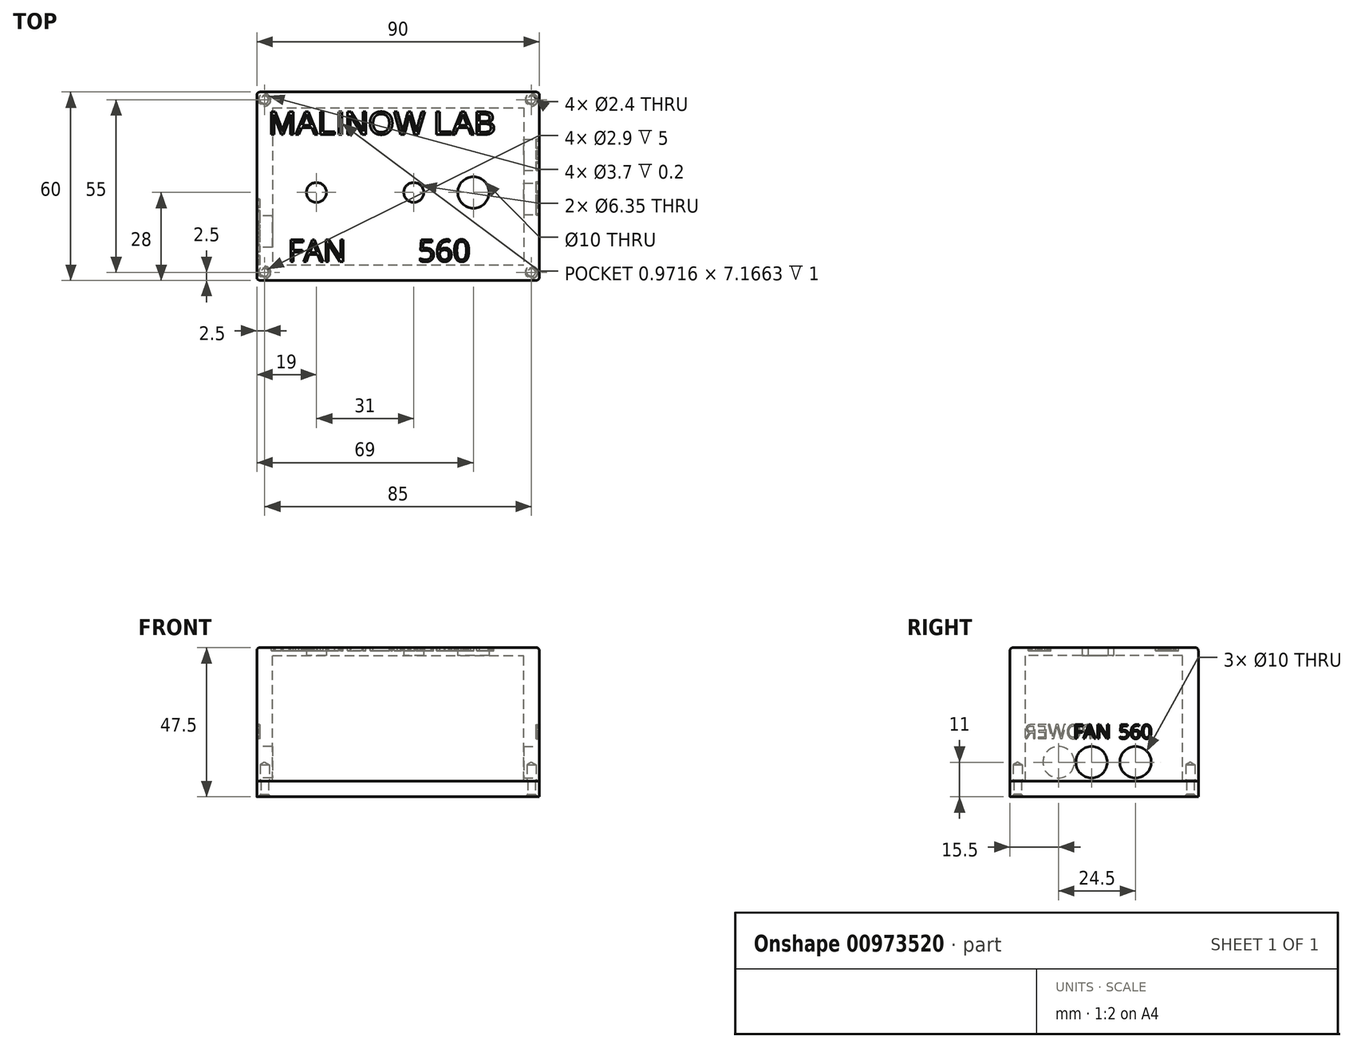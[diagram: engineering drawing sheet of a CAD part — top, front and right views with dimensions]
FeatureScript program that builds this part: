
annotation { "Feature Type Name" : "Feature", "Feature Type Description" : "" }
export const myFeature = defineFeature(function(context is Context, id is Id, definition is map)
    precondition{}
    {
        {
            var Q0;
            Q0=qCreatedBy(makeId("Top.planeOp"),FACE);
            var sketch = newSketch(context, id + "F0", { "sketchPlane" : qUnion([Q0])});
            skLineSegment(sketch, "E0.bottom", {"start": v(0, 0) * mm, "end": v(90, 0) * mm});
            skLineSegment(sketch, "E0.top", {"start": v(0, 60) * mm, "end": v(90, 60) * mm});
            skLineSegment(sketch, "E0.left", {"start": v(0, 0) * mm, "end": v(0, 60) * mm});
            skLineSegment(sketch, "E0.right", {"start": v(90, 0) * mm, "end": v(90, 60) * mm});
            skCircle(sketch, "E1", {"center": v(69, 28) * mm, "radius": 5 * mm});
            skCircle(sketch, "E2", {"center": v(19, 28) * mm, "radius": 3.18 * mm});
            skLineSegment(sketch, "E3", {"start": v(5, 60) * mm, "end": v(5, 5) * mm, "construction": true});
            skLineSegment(sketch, "E4", {"start": v(5, 5) * mm, "end": v(85, 5) * mm, "construction": true});
            skLineSegment(sketch, "E5", {"start": v(85, 5) * mm, "end": v(85, 60) * mm, "construction": true});
            skLineSegment(sketch, "E6", {"start": v(0, 55) * mm, "end": v(90, 55) * mm, "construction": true});
            skLineSegment(sketch, "E7", {"start": v(5, 5) * mm, "end": v(0, 5) * mm, "construction": true});
            skLineSegment(sketch, "E8", {"start": v(85, 5) * mm, "end": v(90, 5) * mm, "construction": true});
            skPoint(sketch, "E9.endSnap0", {"position": v(5, 32.5) * mm});
            skLineSegment(sketch, "E10", {"start": v(5, 60) * mm, "end": v(85, 55) * mm, "construction": true});
            skLineSegment(sketch, "E11", {"start": v(85, 60) * mm, "end": v(5, 55) * mm, "construction": true});
            skLineSegment(sketch, "E12", {"start": v(90, 5) * mm, "end": v(0, 0) * mm, "construction": true});
            skLineSegment(sketch, "E13", {"start": v(0, 5) * mm, "end": v(90, 0) * mm, "construction": true});
            skPoint(sketch, "E14", {"position": v(45, 2.5) * mm});
            skPoint(sketch, "E15", {"position": v(45, 57.5) * mm});
            skLineSegment(sketch, "E16", {"start": v(5, 28) * mm, "end": v(85, 28) * mm, "construction": true});
            skCircle(sketch, "E17", {"center": v(50, 28) * mm, "radius": 3.18 * mm});
            skSolve(sketch);
        }
        {
            var Q0;
            Q0=makeQuery(id+"F0.imprint","IMPRINT",FACE,{"disambiguationData":[TD([[makeQuery(id+"F0.imprint","IMPRINT",EDGE,{"derivedFrom":sQuery(id+"F0.wireOp",EDGE,"E0.bottom")}),1.0]])]});
            extrude(context, id + "F1", {"entities" : qUnion([Q0]), "depth" : 2.5 * mm, "offsetDistance" : 25 * mm});
        }
        {
            var Q0;
            Q0=makeQuery(id+"F1.opExtrude","CAP_FACE",FACE,{"disambiguationData":[OSD([sQuery(id+"F0.wireOp",EDGE,"E0.bottom"),sQuery(id+"F0.wireOp",EDGE,"E0.top"),sQuery(id+"F0.wireOp",EDGE,"E0.left"),sQuery(id+"F0.wireOp",EDGE,"E0.right"),sQuery(id+"F0.wireOp",EDGE,"692mbZP9-ke58-QfXx-eCDH-dWQCKjaEO8YG"),sQuery(id+"F0.wireOp",EDGE,"E1"),sQuery(id+"F0.wireOp",EDGE,"E2")])],"isStart":true});
            var sketch = newSketch(context, id + "F2", { "sketchPlane" : qUnion([Q0])});
            skLineSegment(sketch, "E18.bottom", {"start": v(0, -60) * mm, "end": v(90, -60) * mm, "construction": true});
            skLineSegment(sketch, "E18.top", {"start": v(0, 0) * mm, "end": v(90, 0) * mm, "construction": true});
            skLineSegment(sketch, "E18.left", {"start": v(0, -60) * mm, "end": v(0, 0) * mm, "construction": true});
            skLineSegment(sketch, "E18.right", {"start": v(90, -60) * mm, "end": v(90, 0) * mm, "construction": true});
            skLineSegment(sketch, "E19.bottom", {"start": v(5, -55) * mm, "end": v(85, -55) * mm});
            skLineSegment(sketch, "E19.top", {"start": v(5, -5) * mm, "end": v(85, -5) * mm});
            skLineSegment(sketch, "E19.left", {"start": v(5, -55) * mm, "end": v(5, -5) * mm});
            skLineSegment(sketch, "E19.right", {"start": v(85, -55) * mm, "end": v(85, -5) * mm});
            skSolve(sketch);
        }
        {
            var Q0;
            Q0=makeQuery(id+"F2.imprint","IMPRINT",FACE,{"disambiguationData":[TD([[makeQuery(id+"F2.imprint","IMPRINT",EDGE,{"derivedFrom":sQuery(id+"F2.wireOp",EDGE,"E19.bottom")}),-1.0]])]});
            var Q1;
            Q1=makeQuery(id+"F2.imprint","IMPRINT",FACE,{"disambiguationData":[TD([[makeQuery(id+"F2.imprint","IMPRINT",EDGE,{"derivedFrom":makeQuery(id+"FxvTJw6m9mzOm3c_1.hole-0.boolean.opBoolean","INTERSECT",EDGE,{"derivedFrom":[makeQuery(id+"F1.opExtrude","CAP_FACE",FACE,{"disambiguationData":[OSD([sQuery(id+"F0.wireOp",EDGE,"E0.bottom"),sQuery(id+"F0.wireOp",EDGE,"E0.top"),sQuery(id+"F0.wireOp",EDGE,"E0.left"),sQuery(id+"F0.wireOp",EDGE,"E0.right"),sQuery(id+"F0.wireOp",EDGE,"692mbZP9-ke58-QfXx-eCDH-dWQCKjaEO8YG"),sQuery(id+"F0.wireOp",EDGE,"E1"),sQuery(id+"F0.wireOp",EDGE,"E2")])],"isStart":true}),makeQuery(id+"FxvTJw6m9mzOm3c_1.hole-0.opRevolve","SWEPT_FACE",FACE,{"disambiguationData":[OSD([sQuery(id+"FxvTJw6m9mzOm3c_1.hole-0.sketch.wireOp",EDGE,"core_line_2")])]})]})}),1.0]])]});
            var Q2;
            Q2=makeQuery(id+"F2.imprint","IMPRINT",FACE,{"disambiguationData":[TD([[makeQuery(id+"F2.imprint","IMPRINT",EDGE,{"derivedFrom":makeQuery(id+"FxvTJw6m9mzOm3c_1.hole-1.boolean.opBoolean","INTERSECT",EDGE,{"derivedFrom":[makeQuery(id+"F1.opExtrude","CAP_FACE",FACE,{"disambiguationData":[OSD([sQuery(id+"F0.wireOp",EDGE,"E0.bottom"),sQuery(id+"F0.wireOp",EDGE,"E0.top"),sQuery(id+"F0.wireOp",EDGE,"E0.left"),sQuery(id+"F0.wireOp",EDGE,"E0.right"),sQuery(id+"F0.wireOp",EDGE,"692mbZP9-ke58-QfXx-eCDH-dWQCKjaEO8YG"),sQuery(id+"F0.wireOp",EDGE,"E1"),sQuery(id+"F0.wireOp",EDGE,"E2")])],"isStart":true}),makeQuery(id+"FxvTJw6m9mzOm3c_1.hole-1.opRevolve","SWEPT_FACE",FACE,{"disambiguationData":[OSD([sQuery(id+"FxvTJw6m9mzOm3c_1.hole-1.sketch.wireOp",EDGE,"core_line_2")])]})]})}),1.0]])]});
            var Q3;
            Q3=makeQuery(id+"F2.imprint","IMPRINT",FACE,{"disambiguationData":[TD([[makeQuery(id+"F2.imprint","IMPRINT",EDGE,{"derivedFrom":makeQuery(id+"FxvTJw6m9mzOm3c_1.hole-2.boolean.opBoolean","INTERSECT",EDGE,{"derivedFrom":[makeQuery(id+"F1.opExtrude","CAP_FACE",FACE,{"disambiguationData":[OSD([sQuery(id+"F0.wireOp",EDGE,"E0.bottom"),sQuery(id+"F0.wireOp",EDGE,"E0.top"),sQuery(id+"F0.wireOp",EDGE,"E0.left"),sQuery(id+"F0.wireOp",EDGE,"E0.right"),sQuery(id+"F0.wireOp",EDGE,"692mbZP9-ke58-QfXx-eCDH-dWQCKjaEO8YG"),sQuery(id+"F0.wireOp",EDGE,"E1"),sQuery(id+"F0.wireOp",EDGE,"E2")])],"isStart":true}),makeQuery(id+"FxvTJw6m9mzOm3c_1.hole-2.opRevolve","SWEPT_FACE",FACE,{"disambiguationData":[OSD([sQuery(id+"FxvTJw6m9mzOm3c_1.hole-2.sketch.wireOp",EDGE,"core_line_2")])]})]})}),1.0]])]});
            var Q4;
            Q4=makeQuery(id+"F2.imprint","IMPRINT",FACE,{"disambiguationData":[TD([[makeQuery(id+"F2.imprint","IMPRINT",EDGE,{"derivedFrom":makeQuery(id+"FxvTJw6m9mzOm3c_1.hole-3.boolean.opBoolean","INTERSECT",EDGE,{"derivedFrom":[makeQuery(id+"F1.opExtrude","CAP_FACE",FACE,{"disambiguationData":[OSD([sQuery(id+"F0.wireOp",EDGE,"E0.bottom"),sQuery(id+"F0.wireOp",EDGE,"E0.top"),sQuery(id+"F0.wireOp",EDGE,"E0.left"),sQuery(id+"F0.wireOp",EDGE,"E0.right"),sQuery(id+"F0.wireOp",EDGE,"692mbZP9-ke58-QfXx-eCDH-dWQCKjaEO8YG"),sQuery(id+"F0.wireOp",EDGE,"E1"),sQuery(id+"F0.wireOp",EDGE,"E2")])],"isStart":true}),makeQuery(id+"FxvTJw6m9mzOm3c_1.hole-3.opRevolve","SWEPT_FACE",FACE,{"disambiguationData":[OSD([sQuery(id+"FxvTJw6m9mzOm3c_1.hole-3.sketch.wireOp",EDGE,"core_line_2")])]})]})}),1.0]])]});
            extrude(context, id + "F3", {"entities" : qUnion([Q0, Q1, Q2, Q3, Q4]), "depth" : 40 * mm, "offsetDistance" : 25 * mm});
        }
        {
            var Q0;
            Q0=makeQuery(id+"F3.opExtrude","CAP_FACE",FACE,{"disambiguationData":[OSD([sQuery(id+"F0.wireOp",EDGE,"E0.bottom"),sQuery(id+"F0.wireOp",EDGE,"E0.top"),sQuery(id+"F0.wireOp",EDGE,"E0.left"),sQuery(id+"F0.wireOp",EDGE,"E0.right"),sQuery(id+"F2.wireOp",EDGE,"E19.bottom"),sQuery(id+"F2.wireOp",EDGE,"E19.top"),sQuery(id+"F2.wireOp",EDGE,"E19.left"),sQuery(id+"F2.wireOp",EDGE,"E19.right")])],"isStart":false});
            var sketch = newSketch(context, id + "F4", { "sketchPlane" : qUnion([Q0])});
            skLineSegment(sketch, "E20.bottom", {"start": v(0, 0) * mm, "end": v(90, 0) * mm});
            skLineSegment(sketch, "E20.top", {"start": v(0, -60) * mm, "end": v(90, -60) * mm});
            skLineSegment(sketch, "E20.left", {"start": v(0, 0) * mm, "end": v(0, -60) * mm});
            skLineSegment(sketch, "E20.right", {"start": v(90, 0) * mm, "end": v(90, -60) * mm});
            skLineSegment(sketch, "E21.bottom", {"start": v(5, -5) * mm, "end": v(85, -5) * mm, "construction": true});
            skLineSegment(sketch, "E21.top", {"start": v(5, -55) * mm, "end": v(85, -55) * mm, "construction": true});
            skLineSegment(sketch, "E21.left", {"start": v(5, -5) * mm, "end": v(5, -55) * mm, "construction": true});
            skLineSegment(sketch, "E21.right", {"start": v(85, -5) * mm, "end": v(85, -55) * mm, "construction": true});
            skSolve(sketch);
        }
        {
            var Q0;
            Q0=makeQuery(id+"F4.imprint","IMPRINT",FACE,{"disambiguationData":[TD([[makeQuery(id+"F4.imprint","IMPRINT",EDGE,{"derivedFrom":sQuery(id+"F4.wireOp",EDGE,"E20.bottom")}),-1.0]])]});
            var Q1;
            Q1=makeQuery(id+"F4.imprint","IMPRINT",FACE,{"disambiguationData":[TD([[makeQuery(id+"F4.imprint","IMPRINT",EDGE,{"derivedFrom":makeQuery(id+"F3.opExtrude","CAP_EDGE",EDGE,{"disambiguationData":[OSD([sQuery(id+"F2.wireOp",EDGE,"E19.bottom")])],"isStart":false})}),1.0]])]});
            extrude(context, id + "F5", {"entities" : qUnion([Q0, Q1]), "depth" : 5 * mm, "offsetDistance" : 25 * mm});
        }
        {
            var Q0;
            Q0=makeQuery(id+"F5.opExtrude","CAP_FACE",FACE,{"disambiguationData":[OSD([sQuery(id+"F4.wireOp",EDGE,"E20.bottom"),sQuery(id+"F4.wireOp",EDGE,"E20.top"),sQuery(id+"F4.wireOp",EDGE,"E20.left"),sQuery(id+"F4.wireOp",EDGE,"E20.right")])],"isStart":false});
            var sketch = newSketch(context, id + "F6", { "sketchPlane" : qUnion([Q0])});
            skLineSegment(sketch, "E22.bottom", {"start": v(0, -60) * mm, "end": v(90, -60) * mm, "construction": true});
            skLineSegment(sketch, "E22.top", {"start": v(0, 0) * mm, "end": v(90, 0) * mm, "construction": true});
            skLineSegment(sketch, "E22.left", {"start": v(0, -60) * mm, "end": v(0, 0) * mm, "construction": true});
            skLineSegment(sketch, "E22.right", {"start": v(90, -60) * mm, "end": v(90, 0) * mm, "construction": true});
            skLineSegment(sketch, "E23.bottom", {"start": v(5, -55) * mm, "end": v(85, -55) * mm, "construction": true});
            skLineSegment(sketch, "E23.top", {"start": v(5, -5) * mm, "end": v(85, -5) * mm, "construction": true});
            skLineSegment(sketch, "E23.left", {"start": v(5, -55) * mm, "end": v(5, -5) * mm, "construction": true});
            skLineSegment(sketch, "E23.right", {"start": v(85, -55) * mm, "end": v(85, -5) * mm, "construction": true});
            skLineSegment(sketch, "E24", {"start": v(5, -5) * mm, "end": v(0, 0) * mm, "construction": true});
            skLineSegment(sketch, "E25", {"start": v(85, -5) * mm, "end": v(90, 0) * mm, "construction": true});
            skLineSegment(sketch, "E26", {"start": v(85, -55) * mm, "end": v(90, -60) * mm, "construction": true});
            skLineSegment(sketch, "E27", {"start": v(5, -55) * mm, "end": v(0, -60) * mm, "construction": true});
            skPoint(sketch, "E28", {"position": v(2.5, -2.5) * mm});
            skPoint(sketch, "E29", {"position": v(87.5, -2.5) * mm});
            skPoint(sketch, "E30", {"position": v(87.5, -57.5) * mm});
            skPoint(sketch, "E31", {"position": v(2.5, -57.5) * mm});
            skSolve(sketch);
        }
        {
            var Q0;
            Q0=sQuery(id+"F6.wireOp",VERTEX,"E28");
            var Q1;
            Q1=sQuery(id+"F6.wireOp",VERTEX,"E31");
            var Q2;
            Q2=sQuery(id+"F6.wireOp",VERTEX,"E30");
            var Q3;
            Q3=sQuery(id+"F6.wireOp",VERTEX,"E29");
            var Q4;
            Q4=makeQuery(id+"F3.opExtrude","SWEPT_BODY",BODY,{"disambiguationData":[OSD([sQuery(id+"F0.wireOp",EDGE,"E0.bottom"),sQuery(id+"F0.wireOp",EDGE,"E0.top"),sQuery(id+"F0.wireOp",EDGE,"E0.left"),sQuery(id+"F0.wireOp",EDGE,"E0.right"),sQuery(id+"F2.wireOp",EDGE,"E19.bottom"),sQuery(id+"F2.wireOp",EDGE,"E19.top"),sQuery(id+"F2.wireOp",EDGE,"E19.left"),sQuery(id+"F2.wireOp",EDGE,"E19.right")])]});
            var Q5;
            Q5=makeQuery(id+"F5.opExtrude","SWEPT_BODY",BODY,{"disambiguationData":[OSD([sQuery(id+"F4.wireOp",EDGE,"E20.bottom"),sQuery(id+"F4.wireOp",EDGE,"E20.top"),sQuery(id+"F4.wireOp",EDGE,"E20.left"),sQuery(id+"F4.wireOp",EDGE,"E20.right")])]});
            hole(context, id + "F7", {"style" : HoleStyle.C_SINK, "endStyle" : HoleEndStyle.BLIND, "holeDiameter" : 2.4 * mm, "cSinkDiameter" : 4 * mm, "cSinkAngle" : 90 * degree, "majorDiameter" : 5 * mm, "holeDepth" : 5 * mm, "isTappedThrough" : true, "tappedDepth" : 12 * mm, "tapClearance" : 3, "locations" : qUnion([Q0, Q1, Q2, Q3]), "scope" : qUnion([Q4, Q5])});
        }
        {
            var Q0;
            Q0=makeQuery(id+"F3.opExtrude","CAP_FACE",FACE,{"disambiguationData":[OSD([sQuery(id+"F0.wireOp",EDGE,"E0.bottom"),sQuery(id+"F0.wireOp",EDGE,"E0.top"),sQuery(id+"F0.wireOp",EDGE,"E0.left"),sQuery(id+"F0.wireOp",EDGE,"E0.right"),sQuery(id+"F2.wireOp",EDGE,"E19.bottom"),sQuery(id+"F2.wireOp",EDGE,"E19.top"),sQuery(id+"F2.wireOp",EDGE,"E19.left"),sQuery(id+"F2.wireOp",EDGE,"E19.right")])],"isStart":false});
            var sketch = newSketch(context, id + "F8", { "sketchPlane" : qUnion([Q0])});
            skPoint(sketch, "E32", {"position": v(2.5, -2.5) * mm});
            skPoint(sketch, "E33", {"position": v(2.5, -57.5) * mm});
            skPoint(sketch, "E34", {"position": v(87.5, -57.5) * mm});
            skPoint(sketch, "E35", {"position": v(87.5, -2.5) * mm});
            skSolve(sketch);
        }
        {
            var Q0;
            Q0=sQuery(id+"F8.wireOp",VERTEX,"E32");
            var Q1;
            Q1=sQuery(id+"F8.wireOp",VERTEX,"E33");
            var Q2;
            Q2=sQuery(id+"F8.wireOp",VERTEX,"E34");
            var Q3;
            Q3=sQuery(id+"F8.wireOp",VERTEX,"E35");
            var Q4;
            Q4=makeQuery(id+"F3.opExtrude","SWEPT_BODY",BODY,{"disambiguationData":[OSD([sQuery(id+"F0.wireOp",EDGE,"E0.bottom"),sQuery(id+"F0.wireOp",EDGE,"E0.top"),sQuery(id+"F0.wireOp",EDGE,"E0.left"),sQuery(id+"F0.wireOp",EDGE,"E0.right"),sQuery(id+"F2.wireOp",EDGE,"E19.bottom"),sQuery(id+"F2.wireOp",EDGE,"E19.top"),sQuery(id+"F2.wireOp",EDGE,"E19.left"),sQuery(id+"F2.wireOp",EDGE,"E19.right")])]});
            hole(context, id + "F9", {"style" : HoleStyle.C_BORE, "endStyle" : HoleEndStyle.BLIND, "holeDiameter" : 2.9 * mm, "cBoreDiameter" : 3.7 * mm, "cBoreDepth" : .2 * mm, "majorDiameter" : 5 * mm, "holeDepth" : 5.2 * mm, "isTappedThrough" : true, "tappedDepth" : 12 * mm, "tapClearance" : 3, "locations" : qUnion([Q0, Q1, Q2, Q3]), "scope" : qUnion([Q4])});
        }
        {
            var Q0;
            Q0=makeQuery(id+"F1.opExtrude","CAP_EDGE",EDGE,{"disambiguationData":[OSD([sQuery(id+"F0.wireOp",EDGE,"E0.bottom")])],"isStart":false});
            var Q1;
            Q1=makeQuery(id+"F1.opExtrude","CAP_EDGE",EDGE,{"disambiguationData":[OSD([sQuery(id+"F0.wireOp",EDGE,"E0.left")])],"isStart":false});
            var Q2;
            Q2=makeQuery(id+"F1.opExtrude","CAP_EDGE",EDGE,{"disambiguationData":[OSD([sQuery(id+"F0.wireOp",EDGE,"E0.top")])],"isStart":false});
            var Q3;
            Q3=makeQuery(id+"F1.opExtrude","CAP_EDGE",EDGE,{"disambiguationData":[OSD([sQuery(id+"F0.wireOp",EDGE,"E0.right")])],"isStart":false});
            var Q4;
            Q4=makeQuery(id+"F3.opExtrude","SWEPT_EDGE",EDGE,{"disambiguationData":[OSD([sQuery(id+"F0.wireOp",EDGE,"E0.bottom"),sQuery(id+"F0.wireOp",EDGE,"E0.right")])]});
            var Q5;
            Q5=makeQuery(id+"F3.opExtrude","SWEPT_EDGE",EDGE,{"disambiguationData":[OSD([sQuery(id+"F0.wireOp",EDGE,"E0.bottom"),sQuery(id+"F0.wireOp",EDGE,"E0.left")])]});
            var Q6;
            Q6=makeQuery(id+"F1.opExtrude","SWEPT_EDGE",EDGE,{"disambiguationData":[OSD([sQuery(id+"F0.wireOp",EDGE,"E0.bottom"),sQuery(id+"F0.wireOp",EDGE,"E0.left")])]});
            var Q7;
            Q7=makeQuery(id+"F1.opExtrude","SWEPT_EDGE",EDGE,{"disambiguationData":[OSD([sQuery(id+"F0.wireOp",EDGE,"E0.bottom"),sQuery(id+"F0.wireOp",EDGE,"E0.right")])]});
            var Q8;
            Q8=makeQuery(id+"F3.opExtrude","SWEPT_EDGE",EDGE,{"disambiguationData":[OSD([sQuery(id+"F0.wireOp",EDGE,"E0.top"),sQuery(id+"F0.wireOp",EDGE,"E0.right")])]});
            var Q9;
            Q9=makeQuery(id+"F1.opExtrude","SWEPT_EDGE",EDGE,{"disambiguationData":[OSD([sQuery(id+"F0.wireOp",EDGE,"E0.top"),sQuery(id+"F0.wireOp",EDGE,"E0.right")])]});
            var Q10;
            Q10=makeQuery(id+"F3.opExtrude","SWEPT_EDGE",EDGE,{"disambiguationData":[OSD([sQuery(id+"F0.wireOp",EDGE,"E0.top"),sQuery(id+"F0.wireOp",EDGE,"E0.left")])]});
            var Q11;
            Q11=makeQuery(id+"F1.opExtrude","SWEPT_EDGE",EDGE,{"disambiguationData":[OSD([sQuery(id+"F0.wireOp",EDGE,"E0.top"),sQuery(id+"F0.wireOp",EDGE,"E0.left")])]});
            var Q12;
            Q12=makeQuery(id+"F5.opExtrude","SWEPT_EDGE",EDGE,{"disambiguationData":[OSD([sQuery(id+"F4.wireOp",EDGE,"E20.top"),sQuery(id+"F4.wireOp",EDGE,"E20.left")])]});
            var Q13;
            Q13=makeQuery(id+"F5.opExtrude","SWEPT_EDGE",EDGE,{"disambiguationData":[OSD([sQuery(id+"F4.wireOp",EDGE,"E20.bottom"),sQuery(id+"F4.wireOp",EDGE,"E20.left")])]});
            var Q14;
            Q14=makeQuery(id+"F5.opExtrude","SWEPT_EDGE",EDGE,{"disambiguationData":[OSD([sQuery(id+"F4.wireOp",EDGE,"E20.top"),sQuery(id+"F4.wireOp",EDGE,"E20.right")])]});
            var Q15;
            Q15=makeQuery(id+"F5.opExtrude","SWEPT_EDGE",EDGE,{"disambiguationData":[OSD([sQuery(id+"F4.wireOp",EDGE,"E20.bottom"),sQuery(id+"F4.wireOp",EDGE,"E20.right")])]});
            fillet(context, id + "F10", {"entities" : qUnion([Q0, Q1, Q2, Q3, Q4, Q5, Q6, Q7, Q8, Q9, Q10, Q11, Q12, Q13, Q14, Q15]), "radius" : 1 * mm, "tangentPropagation" : true, "allowEdgeOverflow" : false});
        }
        {
            var Q0;
            Q0=makeQuery(id+"F3.opExtrude","SWEPT_FACE",FACE,{"disambiguationData":[OSD([sQuery(id+"F0.wireOp",EDGE,"E0.left")])]});
            var sketch = newSketch(context, id + "F11", { "sketchPlane" : qUnion([Q0])});
            skCircle(sketch, "E36", {"center": v(-15.5, -34) * mm, "radius": 5 * mm});
            skLineSegment(sketch, "E37", {"start": v(-30, -40) * mm, "end": v(-30, 0) * mm, "construction": true});
            skLineSegment(sketch, "E38", {"start": v(-30, 0) * mm, "end": v(-1, -40) * mm, "construction": true});
            skLineSegment(sketch, "E39", {"start": v(-15.5, -20) * mm, "end": v(-15.5, -40) * mm, "construction": true});
            skLineSegment(sketch, "E40", {"start": v(-15.5, -40) * mm, "end": v(-15.5, 0) * mm, "construction": true});
            skSolve(sketch);
        }
        {
            var Q0;
            Q0=makeQuery(id+"F11.imprint","IMPRINT",FACE,{"disambiguationData":[TD([[makeQuery(id+"F11.imprint","IMPRINT",EDGE,{"derivedFrom":sQuery(id+"F11.wireOp",EDGE,"E36")}),1.0]])]});
            extrude(context, id + "F12", {"entities" : qUnion([Q0]), "operationType" : NewBodyOperationType.REMOVE, "endBound" : BoundingType.UP_TO_NEXT, "oppositeDirection" : true, "depth" : 25 * mm, "offsetDistance" : 25 * mm});
        }
        {
            var Q0;
            Q0=makeQuery(id+"F3.opExtrude","SWEPT_FACE",FACE,{"disambiguationData":[OSD([sQuery(id+"F0.wireOp",EDGE,"E0.right")])]});
            var sketch = newSketch(context, id + "F13", { "sketchPlane" : qUnion([Q0])});
            skLineSegment(sketch, "E41", {"start": v(1, -34) * mm, "end": v(59, -34) * mm, "construction": true});
            skCircle(sketch, "E42", {"center": v(26, -34) * mm, "radius": 5 * mm});
            skCircle(sketch, "E43", {"center": v(40, -34) * mm, "radius": 5 * mm});
            skSolve(sketch);
        }
        {
            var Q0;
            Q0=makeQuery(id+"F13.imprint","IMPRINT",FACE,{"disambiguationData":[TD([[makeQuery(id+"F13.imprint","IMPRINT",EDGE,{"derivedFrom":sQuery(id+"F13.wireOp",EDGE,"E42")}),1.0]])]});
            var Q1;
            Q1=makeQuery(id+"F13.imprint","IMPRINT",FACE,{"disambiguationData":[TD([[makeQuery(id+"F13.imprint","IMPRINT",EDGE,{"derivedFrom":sQuery(id+"F13.wireOp",EDGE,"E43")}),1.0]])]});
            var Q2;
            Q2=makeQuery(id+"F13.imprint","IMPRINT",FACE,{"disambiguationData":[TD([[makeQuery(id+"F13.imprint","IMPRINT",EDGE,{"derivedFrom":sQuery(id+"F13.wireOp",EDGE,"z5ahbYnX-TxnG-AjFd-NFLQ-6TXHqK5QM6zY")}),1.0]])]});
            extrude(context, id + "F14", {"entities" : qUnion([Q0, Q1, Q2]), "operationType" : NewBodyOperationType.REMOVE, "endBound" : BoundingType.UP_TO_NEXT, "oppositeDirection" : true, "depth" : 25 * mm, "offsetDistance" : 25 * mm});
        }
        {
            var Q0;
            Q0=makeQuery(id+"F10.opFillet","SPLIT",FACE,{"disambiguationData":[OD(4.0)],"derivedFrom":makeQuery(id+"F1.opExtrude","CAP_FACE",FACE,{"disambiguationData":[OSD([sQuery(id+"F0.wireOp",EDGE,"E0.bottom"),sQuery(id+"F0.wireOp",EDGE,"E0.top"),sQuery(id+"F0.wireOp",EDGE,"E0.left"),sQuery(id+"F0.wireOp",EDGE,"E0.right"),sQuery(id+"F0.wireOp",EDGE,"692mbZP9-ke58-QfXx-eCDH-dWQCKjaEO8YG"),sQuery(id+"F0.wireOp",EDGE,"E1"),sQuery(id+"F0.wireOp",EDGE,"E2")])],"isStart":false})});
            var sketch = newSketch(context, id + "F15", { "sketchPlane" : qUnion([Q0])});
            skLineSegment(sketch, "E44.bottom", {"start": v(1, 54) * mm, "end": v(89, 54) * mm, "construction": true});
            skLineSegment(sketch, "E44.top", {"start": v(1, 46.5) * mm, "end": v(89, 46.5) * mm, "construction": true});
            skLineSegment(sketch, "E44.left", {"start": v(1, 54) * mm, "end": v(1, 46.5) * mm, "construction": true});
            skLineSegment(sketch, "E44.right", {"start": v(89, 54) * mm, "end": v(89, 46.5) * mm, "construction": true});
            skLineSegment(sketch, "E45", {"start": v(45, 54) * mm, "end": v(45, 46.5) * mm, "construction": true});
            skLineSegment(sketch, "E46.bottom", {"start": v(70.39, 54) * mm, "end": v(8.74, 54) * mm, "construction": true});
            skLineSegment(sketch, "E46.top", {"start": v(81.26, 46.5) * mm, "end": v(19.61, 46.5) * mm, "construction": true});
            skLineSegment(sketch, "E46.left", {"start": v(70.39, 54) * mm, "end": v(81.26, 46.5) * mm, "construction": true});
            skLineSegment(sketch, "E46.right", {"start": v(8.74, 54) * mm, "end": v(19.61, 46.5) * mm, "construction": true});
            skPoint(sketch, "E46.middle", {"position": v(45, 50.25) * mm});
            skText(sketch, "E47", { "text": "MALINOW LAB\n", "fontName": "Arimo-Regular.ttf"});
            const initialGuessF15  = {"E47": [0.00374, 0.0465, 1, 0, 0.0075]};
            skSetInitialGuess(sketch, initialGuessF15);
            skSolve(sketch);
        }
        {
            var Q0;
            Q0=qSketchRegion(id+"F15",true);
            extrude(context, id + "F16", {"entities" : qUnion([Q0]), "operationType" : NewBodyOperationType.REMOVE, "oppositeDirection" : true, "depth" : 1 * mm, "offsetDistance" : 25 * mm});
        }
        {
            var Q0;
            Q0=makeQuery(id+"F3.opExtrude","SWEPT_BODY",BODY,{"disambiguationData":[OSD([sQuery(id+"F0.wireOp",EDGE,"E0.bottom"),sQuery(id+"F0.wireOp",EDGE,"E0.top"),sQuery(id+"F0.wireOp",EDGE,"E0.left"),sQuery(id+"F0.wireOp",EDGE,"E0.right"),sQuery(id+"F2.wireOp",EDGE,"E19.bottom"),sQuery(id+"F2.wireOp",EDGE,"E19.top"),sQuery(id+"F2.wireOp",EDGE,"E19.left"),sQuery(id+"F2.wireOp",EDGE,"E19.right")])]});
            var Q1;
            Q1=makeQuery(id+"F1.opExtrude","SWEPT_BODY",BODY,{"disambiguationData":[OSD([sQuery(id+"F0.wireOp",EDGE,"E0.bottom"),sQuery(id+"F0.wireOp",EDGE,"E0.top"),sQuery(id+"F0.wireOp",EDGE,"E0.left"),sQuery(id+"F0.wireOp",EDGE,"E0.right"),sQuery(id+"F0.wireOp",EDGE,"692mbZP9-ke58-QfXx-eCDH-dWQCKjaEO8YG"),sQuery(id+"F0.wireOp",EDGE,"E1"),sQuery(id+"F0.wireOp",EDGE,"E2")])]});
            booleanBodies(context, id + "F17", {"operationType" : BooleanOperationType.UNION, "tools" : qUnion([Q0, Q1])});
        }
        {
            var Q0;
            {var subQ0=sQuery(id+"F0.wireOp",EDGE,"E0.left");var subQ1=sQuery(id+"F0.wireOp",EDGE,"E0.top");var subQ2=sQuery(id+"F0.wireOp",EDGE,"E0.bottom");var subQ3=sQuery(id+"F0.wireOp",EDGE,"E0.right");var subQ4=sQuery(id+"F0.wireOp",EDGE,"E1");var subQ5=sQuery(id+"F0.wireOp",EDGE,"E2");Q0=makeQuery(id+"F16.boolean.opBoolean","SPLIT",FACE,{"disambiguationData":[TD([makeQuery(id+"F1.opExtrude","SWEPT_FACE",FACE,{"disambiguationData":[OSD([subQ4])]})])],"derivedFrom":makeQuery(id+"F1.opExtrude","CAP_FACE",FACE,{"disambiguationData":[OSD([subQ2,subQ1,subQ0,subQ3,subQ4,subQ5])],"isStart":false})});}
            var sketch = newSketch(context, id + "F18", { "sketchPlane" : qUnion([Q0])});
            skText(sketch, "E48", { "text": "FAN", "fontName": "OpenSans-Regular.ttf"});
            skText(sketch, "E49", { "text": "560", "fontName": "OpenSans-Regular.ttf"});
            skLineSegment(sketch, "E50", {"start": v(19, 24.25) * mm, "end": v(19, 1) * mm, "construction": true});
            skLineSegment(sketch, "E51", {"start": v(59.75, 28) * mm, "end": v(59.75, 1) * mm, "construction": true});
            skPoint(sketch, "E52", {"position": v(19, 28) * mm});
            skLineSegment(sketch, "E53", {"start": v(59.75, 28) * mm, "end": v(50.5, 28) * mm, "construction": true});
            skPoint(sketch, "E54", {"position": v(59.75, 28) * mm});
            skLineSegment(sketch, "E55", {"start": v(59.75, 28) * mm, "end": v(59.75, 28) * mm});
            skLineSegment(sketch, "E56", {"start": v(50.5, 28) * mm, "end": v(69, 28) * mm, "construction": true});
            const initialGuessF18  = {"E48": [0.00991, 0.006, 1, 0, 0.007], "E49": [0.05134, 0.006, 1, 0, 0.007]};
            skSetInitialGuess(sketch, initialGuessF18);
            skSolve(sketch);
        }
        {
            var Q0;
            Q0 = qSketchRegion(id + "F18", true);
            extrude(context, id + "F19", {"entities" : qUnion([Q0]), "operationType" : NewBodyOperationType.REMOVE, "oppositeDirection" : true, "depth" : 1 * mm, "offsetDistance" : 25 * mm});
        }
        {
            var Q0;
            {var subQ0=sQuery(id+"F0.wireOp",EDGE,"E0.right");Q0=makeQuery(id+"F17.opBoolean","MERGE",FACE,{"derivedFrom":[makeQuery(id+"F1.opExtrude","SWEPT_FACE",FACE,{"disambiguationData":[OSD([subQ0])]}),makeQuery(id+"F3.opExtrude","SWEPT_FACE",FACE,{"disambiguationData":[OSD([subQ0])]})]});}
            var sketch = newSketch(context, id + "F20", { "sketchPlane" : qUnion([Q0])});
            skLineSegment(sketch, "E57", {"start": v(26, -34) * mm, "end": v(26, 0) * mm, "construction": true});
            skLineSegment(sketch, "E58", {"start": v(40, -34) * mm, "end": v(40, 0) * mm, "construction": true});
            skText(sketch, "E59", { "text": "FAN\n", "fontName": "OpenSans-Regular.ttf"});
            skText(sketch, "E60", { "text": "560\n", "fontName": "OpenSans-Regular.ttf"});
            const initialGuessF20  = {"E59": [0.02016, -0.0265, 1, 0, 0.0045], "E60": [0.0346, -0.0265, 1, 0, 0.0045]};
            skSetInitialGuess(sketch, initialGuessF20);
            skSolve(sketch);
        }
        {
            var Q0;
            Q0 = qSketchRegion(id + "F20", true);
            extrude(context, id + "F21", {"entities" : qUnion([Q0]), "operationType" : NewBodyOperationType.REMOVE, "oppositeDirection" : true, "depth" : 1 * mm, "offsetDistance" : 25 * mm});
        }
        {
            var Q0;
            {var subQ0=sQuery(id+"F0.wireOp",EDGE,"E0.left");Q0=makeQuery(id+"F17.opBoolean","MERGE",FACE,{"derivedFrom":[makeQuery(id+"F1.opExtrude","SWEPT_FACE",FACE,{"disambiguationData":[OSD([subQ0])]}),makeQuery(id+"F3.opExtrude","SWEPT_FACE",FACE,{"disambiguationData":[OSD([subQ0])]})]});}
            var sketch = newSketch(context, id + "F22", { "sketchPlane" : qUnion([Q0])});
            skLineSegment(sketch, "E61", {"start": v(-15.5, -34) * mm, "end": v(-15.5, 1.5) * mm, "construction": true});
            skText(sketch, "E62", { "text": "POWER", "fontName": "OpenSans-Regular.ttf"});
            const initialGuessF22  = {"E62": [-0.02653, -0.0265, 1, 0, 0.0045]};
            skSetInitialGuess(sketch, initialGuessF22);
            skSolve(sketch);
        }
        {
            var Q0;
            Q0 = qSketchRegion(id + "F22", true);
            extrude(context, id + "F23", {"entities" : qUnion([Q0]), "operationType" : NewBodyOperationType.REMOVE, "oppositeDirection" : true, "depth" : 1 * mm, "offsetDistance" : 25 * mm});
        }
    });
